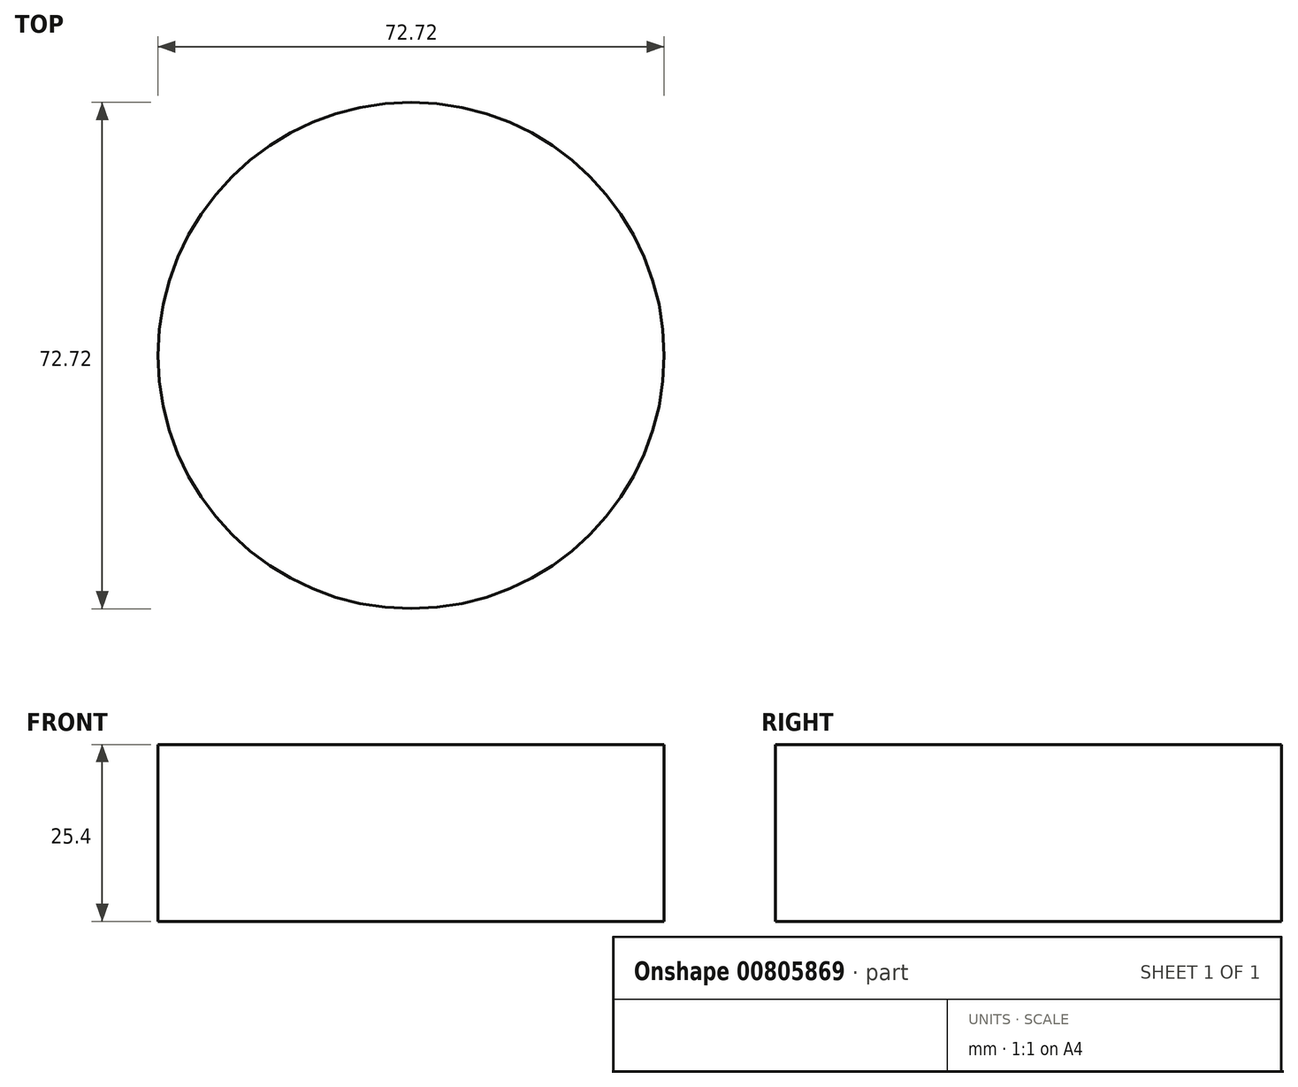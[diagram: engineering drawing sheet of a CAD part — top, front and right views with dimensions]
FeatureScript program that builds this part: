
annotation { "Feature Type Name" : "Feature", "Feature Type Description" : "" }
export const myFeature = defineFeature(function(context is Context, id is Id, definition is map)
    precondition{}
    {
        {
            var Q0;
            Q0=qCreatedBy(makeId("Top.planeOp"),FACE);
            var sketch = newSketch(context, id + "F0", { "sketchPlane" : qUnion([Q0])});
            skCircle(sketch, "E0", {"center": v(0, 0) * mm, "radius": 36.36 * mm});
            skSolve(sketch);
        }
        {
            var Q0;
            Q0 = qSketchRegion(id + "F0", true);
            extrude(context, id + "F1", {"entities" : qUnion([Q0]), "depth" : 25.4 * mm, "offsetDistance" : 25.4 * mm});
        }
    });
